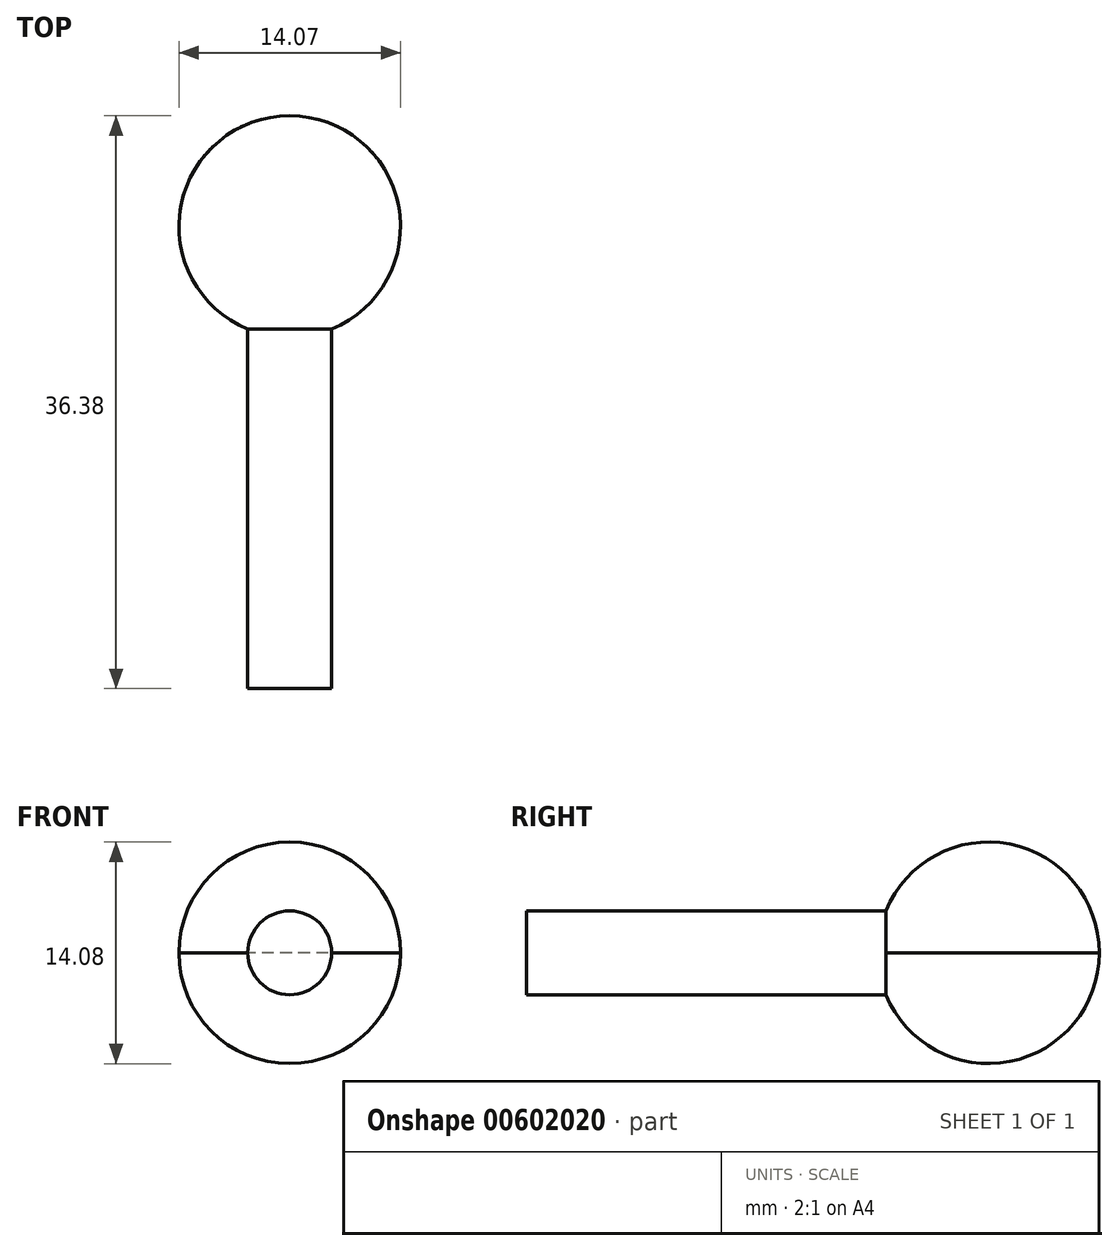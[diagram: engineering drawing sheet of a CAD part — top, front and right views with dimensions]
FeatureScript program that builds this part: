
annotation { "Feature Type Name" : "Feature", "Feature Type Description" : "" }
export const myFeature = defineFeature(function(context is Context, id is Id, definition is map)
    precondition{}
    {
        {
            var Q0;
            Q0=qCreatedBy(makeId("Top.planeOp"),FACE);
            var sketch = newSketch(context, id + "F0", { "sketchPlane" : qUnion([Q0])});
            skLineSegment(sketch, "E0", {"start": v(0, 0) * mm, "end": v(38.1, 0) * mm});
            skLineSegment(sketch, "E1", {"start": v(38.1, 0) * mm, "end": v(38.1, 38.1) * mm});
            skLineSegment(sketch, "E2", {"start": v(38.1, 38.1) * mm, "end": v(0, 38.1) * mm});
            skLineSegment(sketch, "E3", {"start": v(0, 38.1) * mm, "end": v(0, 0) * mm});
            skSolve(sketch);
        }
        {
            var Q0;
            Q0=makeQuery(id+"F0.imprint","IMPRINT",FACE,{"disambiguationData":[TD([[makeQuery(id+"F0.imprint","IMPRINT",EDGE,{"derivedFrom":sQuery(id+"F0.wireOp",EDGE,"E0")}),1.0]])]});
            extrude(context, id + "F1", {"entities" : qUnion([Q0]), "depth" : 0 * mm, "offsetDistance" : 25.4 * mm});
        }
        {
            var Q0;
            Q0=makeQuery(id+"F1.opExtrude","CAP_FACE",FACE,{"disambiguationData":[OSD([sQuery(id+"F0.wireOp",EDGE,"E0"),sQuery(id+"F0.wireOp",EDGE,"E1"),sQuery(id+"F0.wireOp",EDGE,"E2"),sQuery(id+"F0.wireOp",EDGE,"E3")])],"isStart":false});
            var sketch = newSketch(context, id + "F2", { "sketchPlane" : qUnion([Q0])});
            skArc(sketch, "E4", {"start": v(20.07, 36.38) * mm, "mid": v(13.17, 30.7) * mm, "end": v(17.41, 22.83) * mm});
            skLineSegment(sketch, "E5", {"start": v(17.41, 22.83) * mm, "end": v(17.41, 0) * mm});
            skLineSegment(sketch, "E6", {"start": v(22.73, 0) * mm, "end": v(17.41, 0) * mm});
            skLineSegment(sketch, "E7", {"start": v(20.07, 0) * mm, "end": v(20.07, 38.1) * mm});
            skSolve(sketch);
        }
        {
            var Q0;
            Q0 = qSketchRegion(id + "F2", true);
            var Q1;
            Q1=sQuery(id+"F2.wireOp",EDGE,"E7");
            revolve(context, id + "F3", {"operationType" : NewBodyOperationType.ADD, "entities" : qUnion([Q0]), "axis" : qUnion([Q1]), "revolveType" : RevolveType.FULL});
        }
        {
            var Q0;
            Q0=makeQuery(id+"F1.opExtrude","CAP_FACE",FACE,{"disambiguationData":[OSD([sQuery(id+"F0.wireOp",EDGE,"E0"),sQuery(id+"F0.wireOp",EDGE,"E1"),sQuery(id+"F0.wireOp",EDGE,"E2"),sQuery(id+"F0.wireOp",EDGE,"E3")])],"isStart":false});
            extrude(context, id + "F4", {"entities" : qUnion([Q0]), "operationType" : NewBodyOperationType.REMOVE, "oppositeDirection" : true, "depth" : 25.4 * mm, "offsetDistance" : 25.4 * mm});
        }
    });
